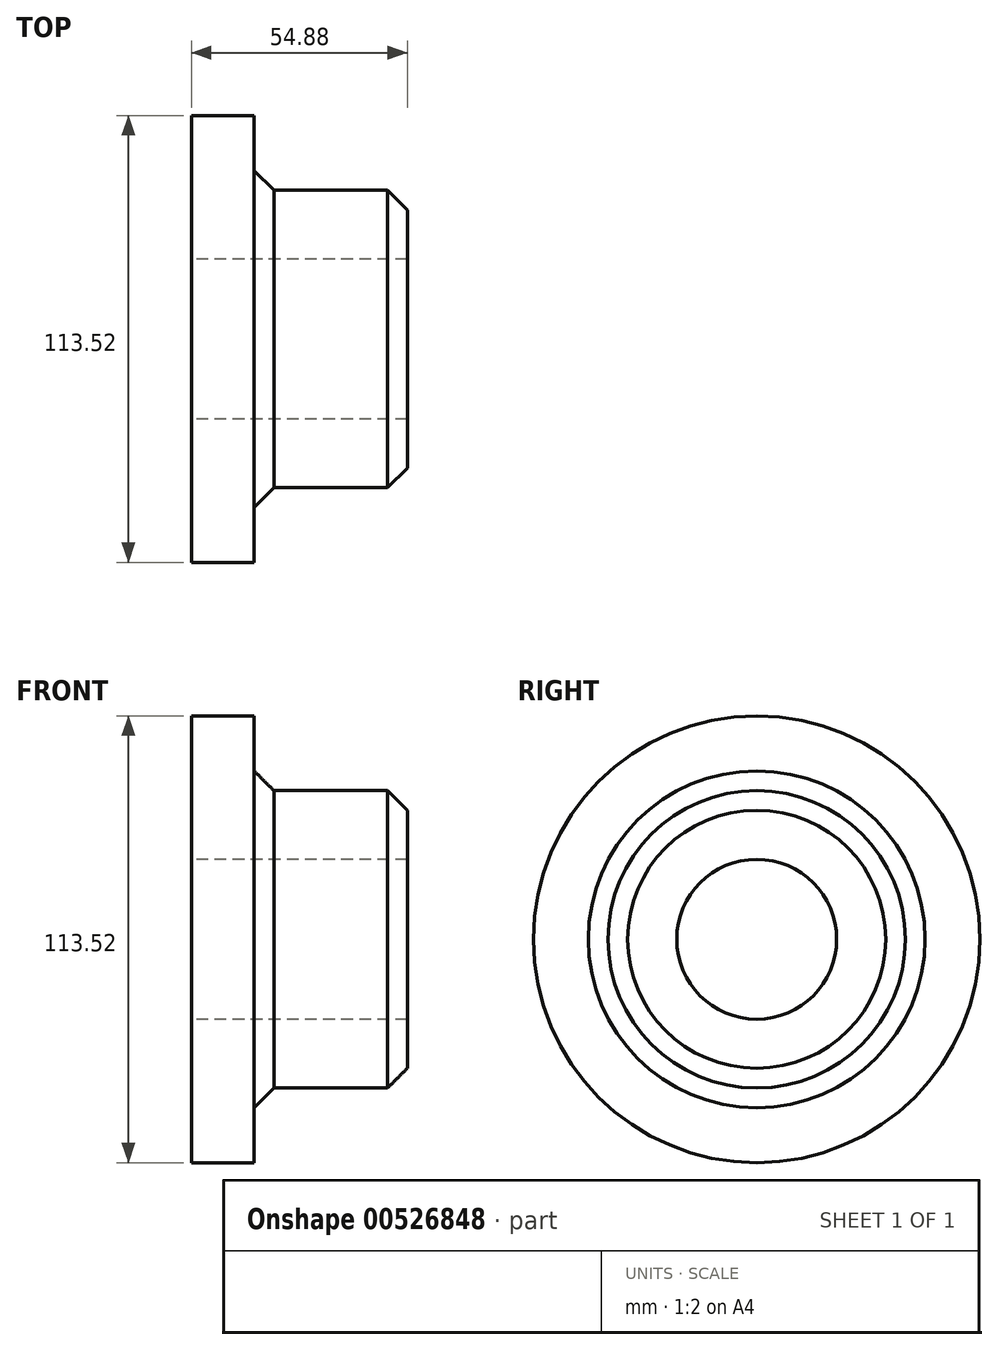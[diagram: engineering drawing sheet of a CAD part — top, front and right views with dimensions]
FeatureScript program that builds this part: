
annotation { "Feature Type Name" : "Feature", "Feature Type Description" : "" }
export const myFeature = defineFeature(function(context is Context, id is Id, definition is map)
    precondition{}
    {
        {
            var Q0;
            Q0=qCreatedBy(makeId("Front.planeOp"),FACE);
            var sketch = newSketch(context, id + "F0", { "sketchPlane" : qUnion([Q0])});
            skLineSegment(sketch, "E0.bottom", {"start": v(0, 37.78) * mm, "end": v(15.98, 37.78) * mm});
            skLineSegment(sketch, "E0.top", {"start": v(0, 56.76) * mm, "end": v(15.98, 56.76) * mm});
            skLineSegment(sketch, "E0.left", {"start": v(0, 37.78) * mm, "end": v(0, 56.76) * mm});
            skLineSegment(sketch, "E0.right", {"start": v(15.98, 37.78) * mm, "end": v(15.98, 56.76) * mm});
            skLineSegment(sketch, "E1.top", {"start": v(0, 20.3) * mm, "end": v(15.98, 20.3) * mm});
            skLineSegment(sketch, "E1.left", {"start": v(0, 37.78) * mm, "end": v(0, 20.3) * mm});
            skLineSegment(sketch, "E1.right", {"start": v(15.98, 37.78) * mm, "end": v(15.98, 20.3) * mm});
            skLineSegment(sketch, "E2.bottom", {"start": v(15.98, 37.78) * mm, "end": v(54.88, 37.78) * mm});
            skLineSegment(sketch, "E2.top", {"start": v(15.98, 20.3) * mm, "end": v(54.88, 20.3) * mm});
            skLineSegment(sketch, "E2.right", {"start": v(54.88, 37.78) * mm, "end": v(54.88, 20.3) * mm});
            skLineSegment(sketch, "E3", {"start": v(0, 0) * mm, "end": v(50.75, 0) * mm});
            skLineSegment(sketch, "E4.MirrorCS", {"start": v(0, -56.76) * mm, "end": v(15.98, -56.76) * mm});
            skLineSegment(sketch, "E5.MirrorCS", {"start": v(0, -37.78) * mm, "end": v(15.98, -37.78) * mm});
            skLineSegment(sketch, "E6.MirrorCS", {"start": v(15.98, -37.78) * mm, "end": v(15.98, -20.3) * mm});
            skLineSegment(sketch, "E7.MirrorCS", {"start": v(0, -37.78) * mm, "end": v(0, -20.3) * mm});
            skLineSegment(sketch, "E8.MirrorCS", {"start": v(0, -37.78) * mm, "end": v(0, -56.76) * mm});
            skLineSegment(sketch, "E9.MirrorCS", {"start": v(0, -20.3) * mm, "end": v(15.98, -20.3) * mm});
            skLineSegment(sketch, "E10.MirrorCS", {"start": v(15.98, -37.78) * mm, "end": v(15.98, -56.76) * mm});
            skLineSegment(sketch, "E11.MirrorCS", {"start": v(54.88, -37.78) * mm, "end": v(54.88, -20.3) * mm});
            skLineSegment(sketch, "E12.MirrorCS", {"start": v(15.98, -20.3) * mm, "end": v(54.88, -20.3) * mm});
            skLineSegment(sketch, "E13.MirrorCS", {"start": v(15.98, -37.78) * mm, "end": v(54.88, -37.78) * mm});
            skSolve(sketch);
        }
        {
            var Q0;
            Q0=makeQuery(id+"F0.imprint","IMPRINT",FACE,{"disambiguationData":[TD([[makeQuery(id+"F0.imprint","IMPRINT",EDGE,{"derivedFrom":sQuery(id+"F0.wireOp",EDGE,"E2.bottom")}),-1.0]])]});
            var Q1;
            Q1=makeQuery(id+"F0.imprint","IMPRINT",FACE,{"disambiguationData":[TD([[makeQuery(id+"F0.imprint","IMPRINT",EDGE,{"derivedFrom":sQuery(id+"F0.wireOp",EDGE,"E0.bottom")}),-1.0]])]});
            var Q2;
            Q2=makeQuery(id+"F0.imprint","IMPRINT",FACE,{"disambiguationData":[TD([[makeQuery(id+"F0.imprint","IMPRINT",EDGE,{"derivedFrom":sQuery(id+"F0.wireOp",EDGE,"E0.top")}),-1.0]])]});
            var Q3;
            Q3=sQuery(id+"F0.wireOp",EDGE,"E3");
            revolve(context, id + "F1", {"entities" : qUnion([Q0, Q1, Q2]), "axis" : qUnion([Q3]), "revolveType" : RevolveType.FULL});
        }
        {
            var Q0;
            Q0=makeQuery(id+"F1.opRevolve","SWEPT_EDGE",EDGE,{"disambiguationData":[OSD([sQuery(id+"F0.wireOp",EDGE,"E0.right"),sQuery(id+"F0.wireOp",EDGE,"E0.bottom"),sQuery(id+"F0.wireOp",EDGE,"E2.bottom"),sQuery(id+"F0.wireOp",EDGE,"E1.right")])]});
            var Q1;
            Q1=makeQuery(id+"F1.opRevolve","SWEPT_EDGE",EDGE,{"disambiguationData":[OSD([sQuery(id+"F0.wireOp",EDGE,"E2.bottom"),sQuery(id+"F0.wireOp",EDGE,"E2.right")])]});
            chamfer(context, id + "F2", {"entities" : qUnion([Q0, Q1]), "width" : 5 * mm, "tangentPropagation" : true});
        }
    });
